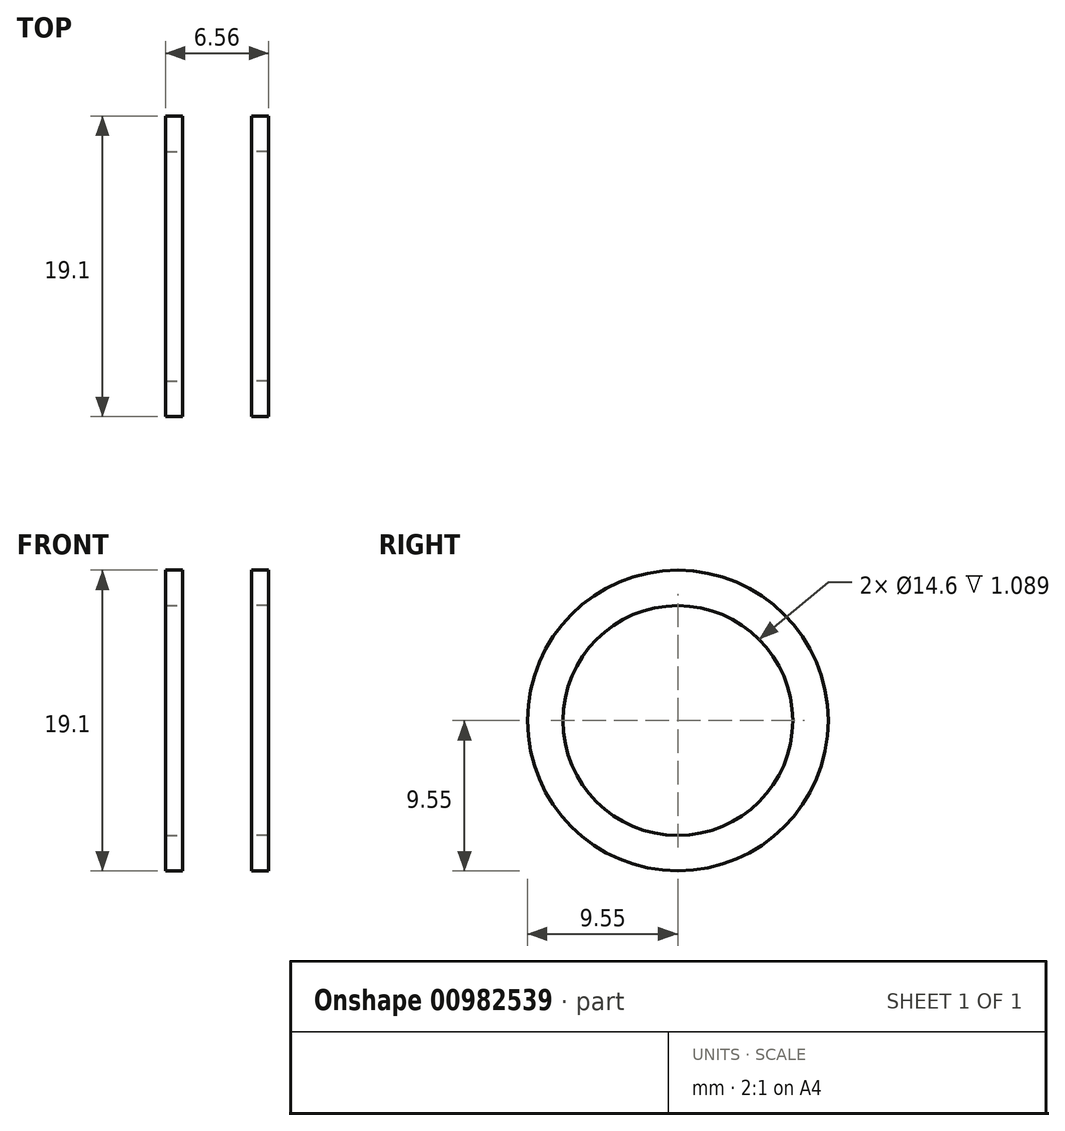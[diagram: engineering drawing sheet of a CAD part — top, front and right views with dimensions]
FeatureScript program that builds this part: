
annotation { "Feature Type Name" : "Feature", "Feature Type Description" : "" }
export const myFeature = defineFeature(function(context is Context, id is Id, definition is map)
    precondition{}
    {
        {
            var Q0;
            Q0=qCreatedBy(makeId("Front.planeOp"),FACE);
            var sketch = newSketch(context, id + "F0", { "sketchPlane" : qUnion([Q0])});
            skLineSegment(sketch, "E0", {"start": v(0, 3.2) * mm, "end": v(0, 1.8) * mm});
            skLineSegment(sketch, "E1", {"start": v(0, 1.8) * mm, "end": v(3.8, 1.8) * mm});
            skFitSpline(sketch, "E2", {"points": [v(3.8, 1.8) * mm, v(5.01, 0) * mm], "startDerivative": vector(1.19, -0.13) * mm, "endDerivative": vector(-0.53, -1.2) * mm});
            skLineSegment(sketch, "E3", {"start": v(0, 3.2) * mm, "end": v(0.8, 3.3) * mm});
            skLineSegment(sketch, "E4", {"start": v(0.8, 3.3) * mm, "end": v(1.41, 3.3) * mm});
            skLineSegment(sketch, "E5", {"start": v(2.9, 4.2) * mm, "end": v(2.9, 6.56) * mm});
            skLineSegment(sketch, "E6", {"start": v(2.9, 6.56) * mm, "end": v(1.87, 6.56) * mm});
            skLineSegment(sketch, "E7", {"start": v(2.26, 7.16) * mm, "end": v(3.28, 7.16) * mm});
            skLineSegment(sketch, "E8", {"start": v(3.28, 7.16) * mm, "end": v(3.28, 9.67) * mm});
            skLineSegment(sketch, "E9", {"start": v(3.28, 9.67) * mm, "end": v(2.16, 9.67) * mm});
            skLineSegment(sketch, "E10", {"start": v(2.16, 9.67) * mm, "end": v(2.16, 10.18) * mm});
            skLineSegment(sketch, "E11", {"start": v(5.01, 0) * mm, "end": v(5.81, 0) * mm});
            skLineSegment(sketch, "E12", {"start": v(1.87, 6.93) * mm, "end": v(2.01, 7.1) * mm});
            skLineSegment(sketch, "E13", {"start": v(2.01, 7.1) * mm, "end": v(2.26, 7.16) * mm});
            skLineSegment(sketch, "E14", {"start": v(1.87, 6.56) * mm, "end": v(1.87, 6.93) * mm});
            skPoint(sketch, "E15", {"position": v(22, 28) * mm});
            skLineSegment(sketch, "E16.MirrorCS", {"start": v(2.08, 3.3) * mm, "end": v(2.08, 4.2) * mm});
            skLineSegment(sketch, "E17.MirrorCS", {"start": v(0.8, 3.3) * mm, "end": v(2.08, 3.3) * mm});
            skFitSpline(sketch, "E18.MirrorCS", {"points": [v(3.8, 1.8) * mm, v(5.01, 0) * mm], "startDerivative": vector(1.19, -0.13) * mm, "endDerivative": vector(-0.53, -1.2) * mm});
            skPoint(sketch, "E19.MirrorP", {"position": v(-22, 28) * mm});
            skLineSegment(sketch, "E20.MirrorCS", {"start": v(2.08, 4.2) * mm, "end": v(2.9, 4.2) * mm});
            skFitSpline(sketch, "E21", {"points": [v(5.81, 0) * mm, v(5.34, 1.37) * mm, v(4.62, 2.38) * mm], "startDerivative": vector(-0.42, 3.1) * mm, "endDerivative": vector(-2.72, 2.46) * mm});
            skLineSegment(sketch, "E22", {"start": v(4.62, 2.38) * mm, "end": v(3.98, 2.89) * mm});
            skLineSegment(sketch, "E23", {"start": v(3.98, 2.89) * mm, "end": v(3.98, 6.23) * mm});
            skLineSegment(sketch, "E24", {"start": v(3.98, 6.23) * mm, "end": v(4.22, 8.04) * mm});
            skLineSegment(sketch, "E25", {"start": v(4.22, 8.04) * mm, "end": v(4.22, 9.73) * mm});
            skLineSegment(sketch, "E26", {"start": v(4.22, 9.73) * mm, "end": v(3.85, 10.24) * mm});
            skLineSegment(sketch, "E27", {"start": v(2.31, 10.71) * mm, "end": v(11.19, 24.87) * mm});
            skLineSegment(sketch, "E28", {"start": v(11.19, 24.87) * mm, "end": v(14.7, 27.38) * mm});
            skLineSegment(sketch, "E29", {"start": v(14.7, 27.38) * mm, "end": v(15.14, 26.42) * mm});
            skLineSegment(sketch, "E30", {"start": v(15.14, 26.42) * mm, "end": v(18.5, 26.42) * mm});
            skLineSegment(sketch, "E31", {"start": v(18.5, 26.42) * mm, "end": v(18.5, 25.94) * mm});
            skLineSegment(sketch, "E32", {"start": v(18.5, 25.94) * mm, "end": v(14.1, 25.94) * mm});
            skLineSegment(sketch, "E33", {"start": v(14.1, 25.94) * mm, "end": v(12.06, 24.5) * mm});
            skLineSegment(sketch, "E34", {"start": v(12.06, 24.5) * mm, "end": v(3.82, 11.35) * mm});
            skPoint(sketch, "E35.visualSharp", {"position": v(3.46, 10.79) * mm});
            skArc(sketch, "E35.filletArc", {"start": v(3.82, 11.35) * mm, "mid": v(3.67, 10.8) * mm, "end": v(3.85, 10.24) * mm});
            skPoint(sketch, "E36.visualSharp", {"position": v(2.16, 10.47) * mm});
            skArc(sketch, "E36.filletArc", {"start": v(2.31, 10.71) * mm, "mid": v(2.2, 10.46) * mm, "end": v(2.16, 10.18) * mm});
            skLineSegment(sketch, "E37", {"start": v(14.7, 27.38) * mm, "end": v(21.35, 27.95) * mm});
            skLineSegment(sketch, "E38", {"start": v(21, 25.96) * mm, "end": v(18.5, 25.94) * mm});
            skLineSegment(sketch, "E39", {"start": v(22, 26.96) * mm, "end": v(22, 27.35) * mm});
            skArc(sketch, "E40.filletArc", {"start": v(22, 27.35) * mm, "mid": v(21.8, 27.79) * mm, "end": v(21.35, 27.95) * mm});
            skPoint(sketch, "E41.visualSharp", {"position": v(22, 25.97) * mm});
            skArc(sketch, "E41.filletArc", {"start": v(21, 25.96) * mm, "mid": v(21.7, 26.26) * mm, "end": v(22, 26.96) * mm});
            skLineSegment(sketch, "E42", {"start": v(2.08, 3.3) * mm, "end": v(0, 3.3) * mm});
            skLineSegment(sketch, "E43", {"start": v(0, 3.3) * mm, "end": v(0, 4.2) * mm});
            skLineSegment(sketch, "E44", {"start": v(0, 4.2) * mm, "end": v(2.08, 4.2) * mm});
            skLineSegment(sketch, "E45", {"start": v(2.08, 6.43) * mm, "end": v(2.08, 5.5) * mm});
            skLineSegment(sketch, "E46", {"start": v(2.08, 5.5) * mm, "end": v(0, 5.5) * mm});
            skLineSegment(sketch, "E47", {"start": v(0, 5.5) * mm, "end": v(0, 6.29) * mm});
            skLineSegment(sketch, "E48", {"start": v(0, 6.29) * mm, "end": v(1.13, 6.29) * mm});
            skLineSegment(sketch, "E49", {"start": v(1.13, 6.29) * mm, "end": v(2.08, 6.43) * mm});
            skLineSegment(sketch, "E50", {"start": v(3.28, 7.3) * mm, "end": v(2.19, 7.3) * mm});
            skLineSegment(sketch, "E51", {"start": v(2.19, 7.3) * mm, "end": v(2.19, 9.55) * mm});
            skLineSegment(sketch, "E52", {"start": v(2.19, 9.55) * mm, "end": v(3.28, 9.55) * mm});
            skSolve(sketch);
        }
        {
            var Q0;
            {var subQ0=sQuery(id+"F0.wireOp",EDGE,"E50");Q0=makeQuery(id+"F0.imprint","IMPRINT",FACE,{"disambiguationData":[TD([[makeQuery(id+"F0.imprint","IMPRINT",EDGE,{"derivedFrom":subQ0}),-1.0]])]});}
            var Q1;
            Q1=sQuery(id+"F0.wireOp",EDGE,"E11");
            revolve(context, id + "F1", {"surfaceOperationType" : NewSurfaceOperationType.NEW, "entities" : qUnion([Q0]), "axis" : qUnion([Q1]), "revolveType" : RevolveType.FULL});
        }
        {
            var Q0;
            Q0=makeQuery(id+"F1.opRevolve","SWEPT_BODY",BODY,{"disambiguationData":[OSD([sQuery(id+"F0.wireOp",EDGE,"E8"),sQuery(id+"F0.wireOp",EDGE,"E50"),sQuery(id+"F0.wireOp",EDGE,"E51"),sQuery(id+"F0.wireOp",EDGE,"E52")])]});
            var Q1;
            Q1=qCreatedBy(makeId("Right.planeOp"),FACE);
            mirror(context, id + "F2", {"operationType" : NewBodyOperationType.ADD, "entities" : qUnion([Q0]), "mirrorPlane" : qUnion([Q1])});
        }
    });
